AUTODESK INVENTOR PART (.ipt)
format: ipt  version: 2020.3 (Build 243373010, 373A)  size: 727,552 bytes
history: native  units: mm
features: fillet x18, extrude x11, sketch x2, chamfer x1, projected_geometry x1
ambient origin geometry x8: Origin, YZ Plane, XZ Plane, XY Plane, X Axis, Y Axis, Z Axis, Center Point
bodies: Solid1 (feature_tree)
feature tree (33):
  extrude  "Extrusion2"  Depth=30.0mm
  extrude  "Extrusion5"  Depth=6.2mm
  extrude  "Extrusion6"  Depth=6.2mm
  sketch  "Sketch4"  dims[d2=4.5mm d9=30.0mm]
  extrude  "Extrusion7"  Depth=6.2mm
  extrude  "Extrusion8"  Depth=6.2mm
  fillet  "Fillet6"  Radius=7.5mm
  chamfer  "Chamfer2"  Distance=3.5mm
  sketch  "Sketch6"  dims[d10=2.2mm d11=15.0mm d12=4.0mm d13=4.0mm d14=15.0mm d15=7.5mm d16=3.5mm d17=2.0mm d18=1.25mm d21=2.4mm d22=0.0mm d38=19.0mm d39=0.0mm d40=2.5mm d41=0.0mm d42=9.0mm d47=13.0mm d49=9.5mm d50=18.0mm d51=0.0mm d52=5.8mm d53=26.0mm d59=7.2mm d60=3.0mm d61=0.0mm d62=18.0mm d65=1.0mm d66=2.0mm d67=2.0mm d68=45.0deg d69=11.0mm d70=9.5mm d71=29.2mm d72=10.0mm d73=0.0mm d74=16.3mm d75=7.6mm d76=19.0mm d77=19.0mm d78=9.5mm d79=11.0mm d81=53.0mm d82=20.0mm d83=20.0mm d84=2.2mm d85=2.0mm d86=46.0mm d87=23.5mm d88=2.0mm d89=2.0mm d90=19.1mm d91=9.55mm d92=12.5mm d93=31.0mm d94=26.0mm d95=35.0mm d96=2.0mm d97=0.0mm d98=4.0mm d99=1.0mm d100=1.0mm d101=9.0mm d103=19.0mm d104=5.0mm d105=6.2mm d106=1.0mm d107=1.0mm d110=1.0mm d111=0.3mm d112=0.4mm d113=2.0mm d114=14.3mm d115=2.0mm d116=0.0mm d117=0.75mm d118=0.0mm d119=1.0mm d120=0.7mm d121=1.0mm d122=3.0mm d123=1.5mm d124=0.0mm d125=1.5mm d126=3.2mm d127=3.2mm d128=12.0mm d129=12.0mm d130=0.8mm d131=0.0mm d132=1.0mm d133=8.25mm d134=0.0mm]
  extrude  "Extrusion9"  Depth=6.2mm
  extrude  "Extrusion10"  Depth=6.2mm
  fillet  "Fillet7"  Radius=2.4mm
  fillet  "Fillet8"  Radius=19.0mm
  fillet  "Fillet9"  Radius=2.5mm
  fillet  "Fillet10"  Radius=9.0mm
  fillet  "Fillet12"  Radius=13.0mm
  fillet  "Fillet13"  Radius=9.5mm
  fillet  "Fillet14"  Radius=18.0mm
  fillet  "Fillet15"  Radius=5.8mm
  fillet  "Fillet16"  Radius=26.0mm
  fillet  "Fillet19"  Radius=7.2mm
  fillet  "Fillet20"  Radius=3.0mm
  fillet  "Fillet21"  Radius=18.0mm
  fillet  "Fillet22"  Radius=1.0mm
  extrude  "Extrusion11"  Depth=6.2mm TaperAngle=45.0deg
  fillet  "Fillet23"  Radius=11.0mm
  fillet  "Fillet24"  Radius=9.5mm
  fillet  "Fillet25"  Radius=29.2mm
  extrude  "Extrusion12"  Depth=10.0mm TaperAngle=0.0deg
  fillet  "Fillet26"  Radius=16.3mm
  extrude  "Extrusion13"  Depth=6.2mm
  extrude  "Extrusion14"  Depth=6.2mm
  projected_geometry  "Projected Loop2"
